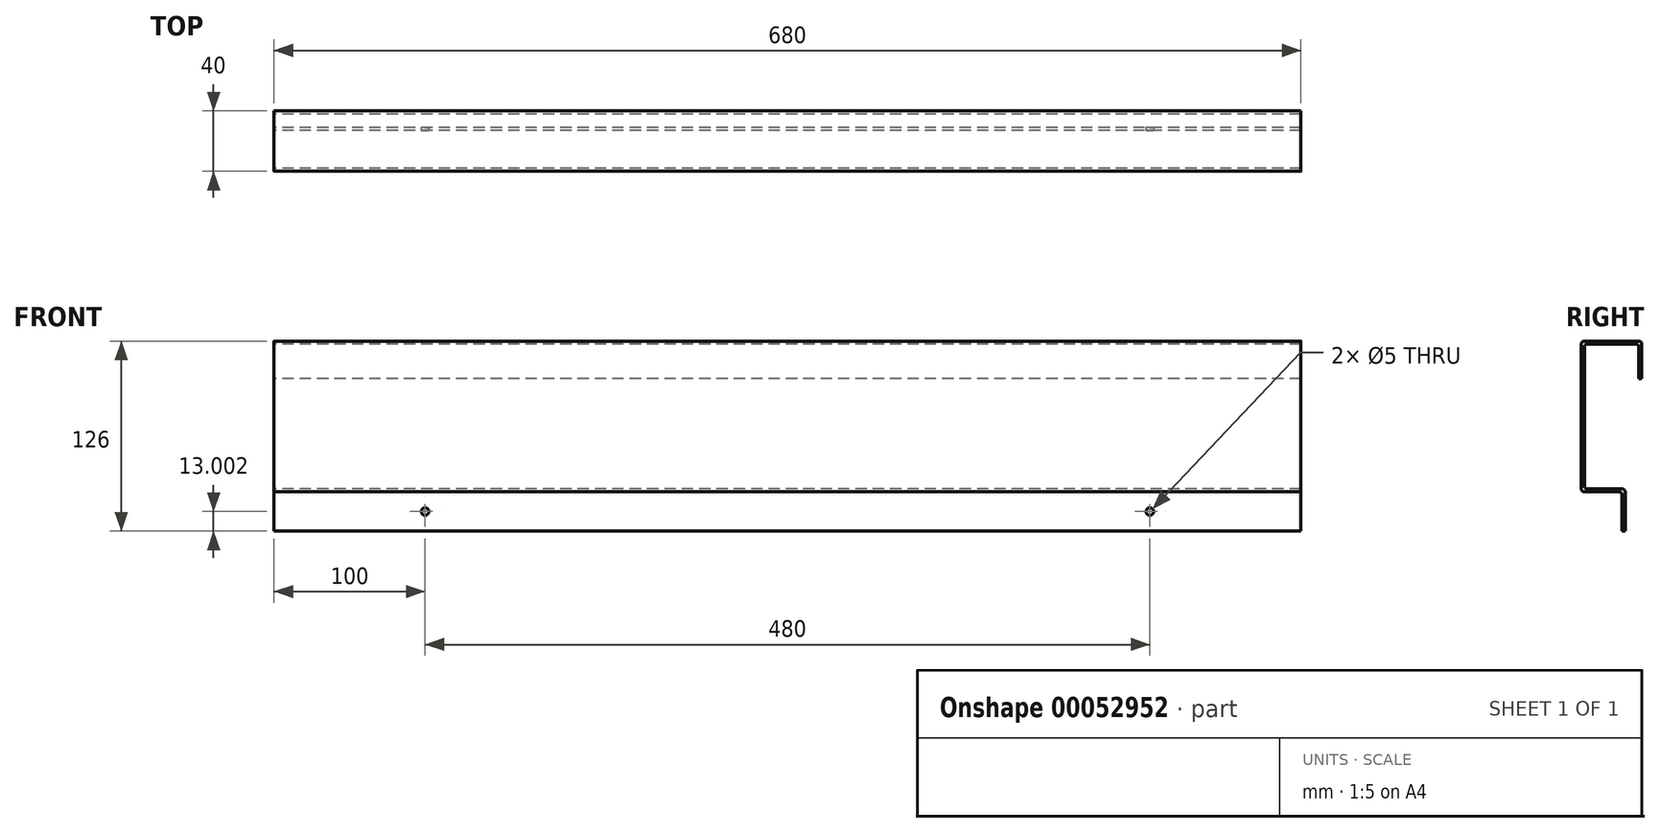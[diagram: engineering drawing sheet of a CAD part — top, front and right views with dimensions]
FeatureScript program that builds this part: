
annotation { "Feature Type Name" : "Feature", "Feature Type Description" : "" }
export const myFeature = defineFeature(function(context is Context, id is Id, definition is map)
    precondition{}
    {
        {
            var Q0;
            Q0=qCreatedBy(makeId("Right.planeOp"),FACE);
            var sketch = newSketch(context, id + "F0", { "sketchPlane" : qUnion([Q0])});
            skLineSegment(sketch, "E0", {"start": v(0, 0) * mm, "end": v(0, 430) * mm, "construction": true});
            skLineSegment(sketch, "E1", {"start": v(0, 0) * mm, "end": v(-250, 0) * mm, "construction": true});
            skLineSegment(sketch, "E2", {"start": v(-18.84, 154.8) * mm, "end": v(-18.84, 177.8) * mm});
            skLineSegment(sketch, "E3", {"start": v(-18.84, 177.8) * mm, "end": v(-54.84, 177.8) * mm});
            skLineSegment(sketch, "E4", {"start": v(-54.84, 177.8) * mm, "end": v(-54.84, 81.8) * mm});
            skLineSegment(sketch, "E5", {"start": v(-54.84, 81.8) * mm, "end": v(-27.84, 81.8) * mm});
            skLineSegment(sketch, "E6.0", {"start": v(-56.84, 79.8) * mm, "end": v(-29.84, 79.8) * mm});
            skLineSegment(sketch, "E6.1", {"start": v(-56.84, 179.8) * mm, "end": v(-56.84, 79.8) * mm});
            skLineSegment(sketch, "E6.2", {"start": v(-16.84, 179.8) * mm, "end": v(-56.84, 179.8) * mm});
            skLineSegment(sketch, "E6.3", {"start": v(-16.84, 154.8) * mm, "end": v(-16.84, 179.8) * mm});
            skLineSegment(sketch, "E7", {"start": v(-27.84, 81.8) * mm, "end": v(-27.84, 53.8) * mm});
            skLineSegment(sketch, "E8", {"start": v(-29.84, 79.8) * mm, "end": v(-29.84, 53.8) * mm});
            skLineSegment(sketch, "E9", {"start": v(-16.84, 154.8) * mm, "end": v(-18.84, 154.8) * mm});
            skLineSegment(sketch, "E10", {"start": v(-27.84, 53.8) * mm, "end": v(-29.84, 53.8) * mm});
            skSolve(sketch);
        }
        {
            var Q0;
            Q0=makeQuery(id+"F0.imprint","IMPRINT",FACE,{"disambiguationData":[TD([[makeQuery(id+"F0.imprint","IMPRINT",EDGE,{"derivedFrom":sQuery(id+"F0.wireOp",EDGE,"97aded3f-c788-494d-ab92-4e00cf807f6c")}),-1.0]])]});
            var Q1;
            Q1=makeQuery(id+"F0.imprint","IMPRINT",FACE,{"disambiguationData":[TD([[makeQuery(id+"F0.imprint","IMPRINT",EDGE,{"derivedFrom":sQuery(id+"F0.wireOp",EDGE,"E2")}),-1.0]])]});
            extrude(context, id + "F1", {"entities" : qUnion([Q0, Q1]), "depth" : 680 * mm});
        }
        {
            var Q0;
            Q0=makeQuery(id+"F1.opExtrude","SWEPT_FACE",FACE,{"disambiguationData":[OSD([sQuery(id+"F0.wireOp",EDGE,"E8")])]});
            var sketch = newSketch(context, id + "F2", { "sketchPlane" : qUnion([Q0])});
            skLineSegment(sketch, "E11", {"start": v(0, 66.8) * mm, "end": v(680, 66.8) * mm});
            skLineSegment(sketch, "E12", {"start": v(580, 79.8) * mm, "end": v(580, 53.8) * mm});
            skPoint(sketch, "E13", {"position": v(580, 66.8) * mm});
            skLineSegment(sketch, "E14", {"start": v(100, 79.8) * mm, "end": v(100, 53.8) * mm});
            skPoint(sketch, "E15", {"position": v(100, 66.8) * mm});
            skSolve(sketch);
        }
        {
            var Q0;
            Q0=sQuery(id+"F2.wireOp",VERTEX,"497ec98f-e9a9-425a-b2b5-6f80ccc2b2cc");
            var Q1;
            Q1=sQuery(id+"F2.wireOp",VERTEX,"82ee78c0-7a07-4074-a8d9-4abe993744e3");
            var Q2;
            Q2=sQuery(id+"F2.wireOp",VERTEX,"E13");
            var Q3;
            Q3=sQuery(id+"F2.wireOp",VERTEX,"E15");
            var Q4;
            Q4=makeQuery(id+"F1.opExtrude","SWEPT_BODY",BODY,{"disambiguationData":[OSD([sQuery(id+"F0.wireOp",EDGE,"E2"),sQuery(id+"F0.wireOp",EDGE,"E3"),sQuery(id+"F0.wireOp",EDGE,"E4"),sQuery(id+"F0.wireOp",EDGE,"E5"),sQuery(id+"F0.wireOp",EDGE,"E6.0"),sQuery(id+"F0.wireOp",EDGE,"E6.1"),sQuery(id+"F0.wireOp",EDGE,"E6.2"),sQuery(id+"F0.wireOp",EDGE,"E6.3"),sQuery(id+"F0.wireOp",EDGE,"E7"),sQuery(id+"F0.wireOp",EDGE,"E8"),sQuery(id+"F0.wireOp",EDGE,"E9"),sQuery(id+"F0.wireOp",EDGE,"E10")])]});
            hole(context, id + "F3", {"style" : HoleStyle.SIMPLE, "holeDiameter" : 5 * mm, "endStyle" : HoleEndStyle.THROUGH, "locations" : qUnion([Q0, Q1, Q2, Q3]), "scope" : qUnion([Q4])});
        }
        {
            var Q0;
            Q0=makeQuery(id+"F1.opExtrude","SWEPT_EDGE",EDGE,{"disambiguationData":[OSD([sQuery(id+"F0.wireOp",EDGE,"E6.1"),sQuery(id+"F0.wireOp",EDGE,"E6.2")])]});
            var Q1;
            Q1=makeQuery(id+"F1.opExtrude","SWEPT_EDGE",EDGE,{"disambiguationData":[OSD([sQuery(id+"F0.wireOp",EDGE,"E6.2"),sQuery(id+"F0.wireOp",EDGE,"E6.3")])]});
            var Q2;
            Q2=makeQuery(id+"F1.opExtrude","SWEPT_EDGE",EDGE,{"disambiguationData":[OSD([sQuery(id+"F0.wireOp",EDGE,"E6.0"),sQuery(id+"F0.wireOp",EDGE,"E6.1")])]});
            var Q3;
            Q3=makeQuery(id+"F1.opExtrude","SWEPT_EDGE",EDGE,{"disambiguationData":[OSD([sQuery(id+"F0.wireOp",EDGE,"E5"),sQuery(id+"F0.wireOp",EDGE,"E7")])]});
            var Q4;
            Q4=makeQuery(id+"F1.opExtrude","SWEPT_EDGE",EDGE,{"disambiguationData":[OSD([sQuery(id+"F0.wireOp",EDGE,"E4"),sQuery(id+"F0.wireOp",EDGE,"E5")])]});
            var Q5;
            Q5=makeQuery(id+"F1.opExtrude","SWEPT_EDGE",EDGE,{"disambiguationData":[OSD([sQuery(id+"F0.wireOp",EDGE,"E6.0"),sQuery(id+"F0.wireOp",EDGE,"E8")])]});
            var Q6;
            Q6=makeQuery(id+"F1.opExtrude","SWEPT_EDGE",EDGE,{"disambiguationData":[OSD([sQuery(id+"F0.wireOp",EDGE,"E2"),sQuery(id+"F0.wireOp",EDGE,"E3")])]});
            var Q7;
            Q7=makeQuery(id+"F1.opExtrude","SWEPT_EDGE",EDGE,{"disambiguationData":[OSD([sQuery(id+"F0.wireOp",EDGE,"E3"),sQuery(id+"F0.wireOp",EDGE,"E4")])]});
            fillet(context, id + "F4", {"entities" : qUnion([Q0, Q1, Q2, Q3, Q4, Q5, Q6, Q7]), "radius" : 2 * mm, "tangentPropagation" : true, "allowEdgeOverflow" : false});
        }
    });
